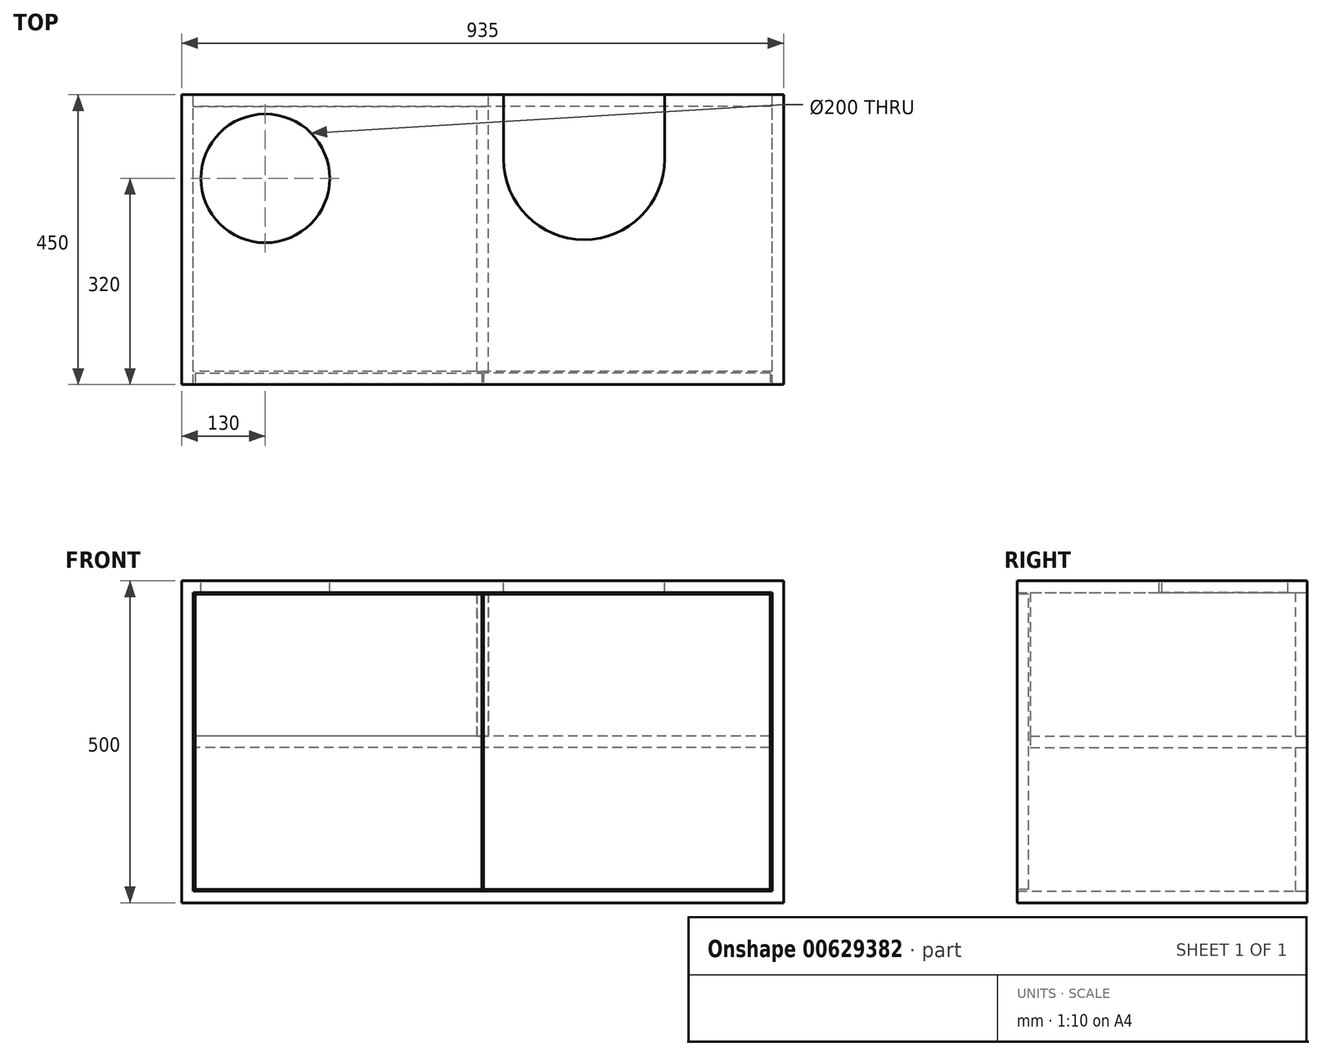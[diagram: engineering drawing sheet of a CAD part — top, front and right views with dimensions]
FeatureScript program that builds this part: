
annotation { "Feature Type Name" : "Feature", "Feature Type Description" : "" }
export const myFeature = defineFeature(function(context is Context, id is Id, definition is map)
    precondition{}
    {
        {
            var Q0;
            Q0=qCreatedBy(makeId("Front.planeOp"),FACE);
            var sketch = newSketch(context, id + "F0", { "sketchPlane" : qUnion([Q0])});
            skLineSegment(sketch, "E0.bottom", {"start": v(-467.5, 250) * mm, "end": v(467.5, 250) * mm});
            skLineSegment(sketch, "E0.top", {"start": v(-467.5, -250) * mm, "end": v(467.5, -250) * mm});
            skLineSegment(sketch, "E0.left", {"start": v(-467.5, 250) * mm, "end": v(-467.5, -250) * mm});
            skLineSegment(sketch, "E0.right", {"start": v(467.5, 250) * mm, "end": v(467.5, -250) * mm});
            skPoint(sketch, "E0.middle", {"position": v(0, 0) * mm});
            skLineSegment(sketch, "E1.0", {"start": v(449.5, 232) * mm, "end": v(449.5, -232) * mm});
            skLineSegment(sketch, "E1.1", {"start": v(-449.5, 232) * mm, "end": v(449.5, 232) * mm});
            skLineSegment(sketch, "E1.2", {"start": v(-449.5, 232) * mm, "end": v(-449.5, -232) * mm});
            skLineSegment(sketch, "E1.3", {"start": v(-449.5, -232) * mm, "end": v(449.5, -232) * mm});
            skSolve(sketch);
        }
        {
            var Q0;
            Q0 = qSketchRegion(id + "F0", true);
            extrude(context, id + "F1", {"entities" : qUnion([Q0]), "depth" : 450 * mm, "offsetDistance" : 25 * mm});
        }
        {
            var Q0;
            Q0=makeQuery(id+"F1.opExtrude","CAP_FACE",FACE,{"disambiguationData":[OSD([sQuery(id+"F0.wireOp",EDGE,"E0.bottom"),sQuery(id+"F0.wireOp",EDGE,"E0.top"),sQuery(id+"F0.wireOp",EDGE,"E0.left"),sQuery(id+"F0.wireOp",EDGE,"E0.right"),sQuery(id+"F0.wireOp",EDGE,"E1.0"),sQuery(id+"F0.wireOp",EDGE,"E1.1"),sQuery(id+"F0.wireOp",EDGE,"E1.2"),sQuery(id+"F0.wireOp",EDGE,"E1.3")])],"isStart":true});
            var sketch = newSketch(context, id + "F2", { "sketchPlane" : qUnion([Q0])});
            skLineSegment(sketch, "E2", {"start": v(-449.5, 0) * mm, "end": v(449.5, 0) * mm, "construction": true});
            skLineSegment(sketch, "E3.bottom", {"start": v(-449.5, 9) * mm, "end": v(449.5, 9) * mm});
            skLineSegment(sketch, "E3.top", {"start": v(-449.5, -9) * mm, "end": v(449.5, -9) * mm});
            skLineSegment(sketch, "E3.left", {"start": v(-449.5, 9) * mm, "end": v(-449.5, -9) * mm});
            skLineSegment(sketch, "E3.right", {"start": v(449.5, 9) * mm, "end": v(449.5, -9) * mm});
            skPoint(sketch, "E3.middle", {"position": v(0, 0) * mm});
            skSolve(sketch);
        }
        {
            var Q0;
            Q0 = qSketchRegion(id + "F2", true);
            extrude(context, id + "F3", {"entities" : qUnion([Q0]), "operationType" : NewBodyOperationType.ADD, "oppositeDirection" : true, "depth" : 430 * mm, "offsetDistance" : 25 * mm});
        }
        {
            var Q0;
            Q0=makeQuery(id+"F1.opExtrude","SWEPT_FACE",FACE,{"disambiguationData":[OSD([sQuery(id+"F0.wireOp",EDGE,"E0.bottom")])]});
            var sketch = newSketch(context, id + "F4", { "sketchPlane" : qUnion([Q0])});
            skCircle(sketch, "E4", {"center": v(-337.5, -130) * mm, "radius": 100 * mm});
            skSolve(sketch);
        }
        {
            var Q0;
            Q0 = qSketchRegion(id + "F4", true);
            var Q1;
            Q1=makeQuery(id+"F1.opExtrude","SWEPT_FACE",FACE,{"disambiguationData":[OSD([sQuery(id+"F0.wireOp",EDGE,"E1.1")])]});
            extrude(context, id + "F5", {"entities" : qUnion([Q0]), "operationType" : NewBodyOperationType.REMOVE, "endBound" : BoundingType.UP_TO_SURFACE, "oppositeDirection" : true, "depth" : 25 * mm, "endBoundEntityFace" : qUnion([Q1]), "offsetDistance" : 25 * mm});
        }
        {
            var Q0;
            Q0=makeQuery(id+"F1.opExtrude","SWEPT_FACE",FACE,{"disambiguationData":[OSD([sQuery(id+"F0.wireOp",EDGE,"E0.bottom")])]});
            var sketch = newSketch(context, id + "F6", { "sketchPlane" : qUnion([Q0])});
            skLineSegment(sketch, "E5", {"start": v(157.5, 0) * mm, "end": v(157.5, -200) * mm, "construction": true});
            skLineSegment(sketch, "E6", {"start": v(257.5, 0) * mm, "end": v(257.5, -60) * mm, "construction": true});
            skLineSegment(sketch, "E7", {"start": v(57.5, 0) * mm, "end": v(57.5, -60) * mm, "construction": true});
            skArc(sketch, "E8", {"start": v(132.5, -200) * mm, "mid": v(157.5, -225) * mm, "end": v(182.5, -200) * mm, "construction": true});
            skArc(sketch, "E9", {"start": v(232.5, -60) * mm, "mid": v(257.5, -85) * mm, "end": v(282.5, -60) * mm, "construction": true});
            skArc(sketch, "E10", {"start": v(32.5, -60) * mm, "mid": v(57.5, -85) * mm, "end": v(82.5, -60) * mm, "construction": true});
            skLineSegment(sketch, "E11", {"start": v(132.5, -200) * mm, "end": v(182.5, -200) * mm, "construction": true});
            skLineSegment(sketch, "E12", {"start": v(232.5, -60) * mm, "end": v(282.5, -60) * mm, "construction": true});
            skLineSegment(sketch, "E13", {"start": v(32.5, -60) * mm, "end": v(82.5, -60) * mm, "construction": true});
            skLineSegment(sketch, "E14", {"start": v(32.5, 0) * mm, "end": v(32.5, -60) * mm, "construction": true});
            skLineSegment(sketch, "E15", {"start": v(82.5, -60) * mm, "end": v(82.5, 0) * mm, "construction": true});
            skLineSegment(sketch, "E16", {"start": v(82.5, 0) * mm, "end": v(32.5, 0) * mm, "construction": true});
            skLineSegment(sketch, "E17", {"start": v(232.5, -60) * mm, "end": v(232.5, 0) * mm, "construction": true});
            skLineSegment(sketch, "E18", {"start": v(232.5, 0) * mm, "end": v(282.5, 0) * mm, "construction": true});
            skLineSegment(sketch, "E19", {"start": v(282.5, 0) * mm, "end": v(282.5, -60) * mm, "construction": true});
            skLineSegment(sketch, "E20", {"start": v(132.5, -200) * mm, "end": v(132.5, 0) * mm, "construction": true});
            skLineSegment(sketch, "E21", {"start": v(132.5, 0) * mm, "end": v(182.5, 0) * mm, "construction": true});
            skLineSegment(sketch, "E22", {"start": v(182.5, 0) * mm, "end": v(182.5, -200) * mm, "construction": true});
            skPoint(sketch, "E23.orphan", {"position": v(257.5, -85) * mm});
            skPoint(sketch, "E24.start.orphan", {"position": v(57.5, -85) * mm});
            skLineSegment(sketch, "E25", {"start": v(32.5, 0) * mm, "end": v(32.5, -60) * mm});
            skLineSegment(sketch, "E26", {"start": v(282.5, -60) * mm, "end": v(282.5, 0) * mm});
            skLineSegment(sketch, "E27", {"start": v(282.5, 0) * mm, "end": v(32.5, 0) * mm});
            skPoint(sketch, "E28.orphan", {"position": v(157.5, -225) * mm});
            skArc(sketch, "E29", {"start": v(32.5, -100) * mm, "mid": v(157.5, -225) * mm, "end": v(282.5, -100) * mm});
            skLineSegment(sketch, "E30", {"start": v(32.5, -60) * mm, "end": v(32.5, -100) * mm});
            skLineSegment(sketch, "E31", {"start": v(282.5, -60) * mm, "end": v(282.5, -100) * mm});
            skSolve(sketch);
        }
        {
            var Q0;
            Q0 = qSketchRegion(id + "F6", true);
            var Q1;
            Q1=makeQuery(id+"F1.opExtrude","SWEPT_FACE",FACE,{"disambiguationData":[OSD([sQuery(id+"F0.wireOp",EDGE,"E1.1")])]});
            extrude(context, id + "F7", {"entities" : qUnion([Q0]), "operationType" : NewBodyOperationType.REMOVE, "endBound" : BoundingType.UP_TO_SURFACE, "oppositeDirection" : true, "depth" : 25 * mm, "endBoundEntityFace" : qUnion([Q1]), "offsetDistance" : 25 * mm});
        }
        {
            var Q0;
            Q0=makeQuery(id+"F1.opExtrude","CAP_FACE",FACE,{"disambiguationData":[OSD([sQuery(id+"F0.wireOp",EDGE,"E0.bottom"),sQuery(id+"F0.wireOp",EDGE,"E0.top"),sQuery(id+"F0.wireOp",EDGE,"E0.left"),sQuery(id+"F0.wireOp",EDGE,"E0.right"),sQuery(id+"F0.wireOp",EDGE,"E1.0"),sQuery(id+"F0.wireOp",EDGE,"E1.1"),sQuery(id+"F0.wireOp",EDGE,"E1.2"),sQuery(id+"F0.wireOp",EDGE,"E1.3")])],"isStart":false});
            var sketch = newSketch(context, id + "F8", { "sketchPlane" : qUnion([Q0])});
            skLineSegment(sketch, "E32.0", {"start": v(-446.5, 229) * mm, "end": v(-446.5, -229) * mm, "construction": true});
            skLineSegment(sketch, "E32.1", {"start": v(-446.5, 229) * mm, "end": v(446.5, 229) * mm, "construction": true});
            skLineSegment(sketch, "E32.2", {"start": v(446.5, 229) * mm, "end": v(446.5, -229) * mm, "construction": true});
            skLineSegment(sketch, "E32.3", {"start": v(-446.5, -229) * mm, "end": v(446.5, -229) * mm, "construction": true});
            skLineSegment(sketch, "E33.bottom", {"start": v(446.5, -229) * mm, "end": v(1.5, -229) * mm});
            skLineSegment(sketch, "E33.top", {"start": v(446.5, 229) * mm, "end": v(1.5, 229) * mm});
            skLineSegment(sketch, "E33.left", {"start": v(446.5, -229) * mm, "end": v(446.5, 229) * mm});
            skLineSegment(sketch, "E33.right", {"start": v(1.5, -229) * mm, "end": v(1.5, 229) * mm});
            skLineSegment(sketch, "E34.bottom", {"start": v(-446.5, -229) * mm, "end": v(-1.5, -229) * mm});
            skLineSegment(sketch, "E34.top", {"start": v(-446.5, 229) * mm, "end": v(-1.5, 229) * mm});
            skLineSegment(sketch, "E34.left", {"start": v(-446.5, -229) * mm, "end": v(-446.5, 229) * mm});
            skLineSegment(sketch, "E34.right", {"start": v(-1.5, -229) * mm, "end": v(-1.5, 229) * mm});
            skLineSegment(sketch, "E35", {"start": v(0, 250) * mm, "end": v(0, -250) * mm, "construction": true});
            skSolve(sketch);
        }
        {
            var Q0;
            Q0 = qSketchRegion(id + "F8", true);
            extrude(context, id + "F9", {"entities" : qUnion([Q0]), "oppositeDirection" : true, "depth" : 18 * mm, "offsetDistance" : 25 * mm});
        }
        {
            var Q0;
            Q0=makeQuery(id+"F3.boolean.opBoolean","MERGE",FACE,{"derivedFrom":[makeQuery(id+"F1.opExtrude","CAP_FACE",FACE,{"disambiguationData":[OSD([sQuery(id+"F0.wireOp",EDGE,"E0.bottom"),sQuery(id+"F0.wireOp",EDGE,"E0.top"),sQuery(id+"F0.wireOp",EDGE,"E0.left"),sQuery(id+"F0.wireOp",EDGE,"E0.right"),sQuery(id+"F0.wireOp",EDGE,"E1.0"),sQuery(id+"F0.wireOp",EDGE,"E1.1"),sQuery(id+"F0.wireOp",EDGE,"E1.2"),sQuery(id+"F0.wireOp",EDGE,"E1.3")])],"isStart":true}),makeQuery(id+"F3.opExtrude","CAP_FACE",FACE,{"disambiguationData":[OSD([sQuery(id+"F2.wireOp",EDGE,"E3.bottom"),sQuery(id+"F2.wireOp",EDGE,"E3.top"),sQuery(id+"F2.wireOp",EDGE,"E3.left"),sQuery(id+"F2.wireOp",EDGE,"E3.right")])],"isStart":true})]});
            var sketch = newSketch(context, id + "F10", { "sketchPlane" : qUnion([Q0])});
            skLineSegment(sketch, "E36.bottom", {"start": v(449.5, -232) * mm, "end": v(-449.5, -232) * mm});
            skLineSegment(sketch, "E36.top", {"start": v(449.5, -9) * mm, "end": v(-449.5, -9) * mm});
            skLineSegment(sketch, "E36.left", {"start": v(449.5, -232) * mm, "end": v(449.5, -9) * mm});
            skLineSegment(sketch, "E36.right", {"start": v(-449.5, -232) * mm, "end": v(-449.5, -9) * mm});
            skPoint(sketch, "E37.startSnap0", {"position": v(0, 9) * mm});
            skPoint(sketch, "E38.orphan", {"position": v(9, 9) * mm});
            skPoint(sketch, "E39.top.start.orphan", {"position": v(-9, 9) * mm});
            skPoint(sketch, "E37.start.orphan", {"position": v(0, -250) * mm});
            skLineSegment(sketch, "E40", {"start": v(0, -250) * mm, "end": v(0, 232) * mm, "construction": true});
            skLineSegment(sketch, "E41", {"start": v(-9, 9) * mm, "end": v(-9, 232) * mm, "construction": true});
            skLineSegment(sketch, "E42.bottom", {"start": v(-9, 232) * mm, "end": v(449.5, 232) * mm});
            skLineSegment(sketch, "E42.top", {"start": v(-9, 9) * mm, "end": v(449.5, 9) * mm});
            skLineSegment(sketch, "E42.left", {"start": v(-9, 232) * mm, "end": v(-9, 9) * mm});
            skLineSegment(sketch, "E42.right", {"start": v(449.5, 232) * mm, "end": v(449.5, 9) * mm});
            skSolve(sketch);
        }
        {
            var Q0;
            Q0 = qSketchRegion(id + "F10", true);
            extrude(context, id + "F11", {"entities" : qUnion([Q0]), "oppositeDirection" : true, "depth" : 18 * mm, "offsetDistance" : 25 * mm});
        }
        {
            var Q0;
            Q0=makeQuery(id+"F11.opExtrude","CAP_FACE",FACE,{"disambiguationData":[OSD([sQuery(id+"F10.wireOp",EDGE,"E42.bottom"),sQuery(id+"F10.wireOp",EDGE,"E42.top"),sQuery(id+"F10.wireOp",EDGE,"E42.left"),sQuery(id+"F10.wireOp",EDGE,"E42.right")])],"isStart":false});
            var sketch = newSketch(context, id + "F12", { "sketchPlane" : qUnion([Q0])});
            skLineSegment(sketch, "E43.bottom", {"start": v(-9, 9) * mm, "end": v(9, 9) * mm});
            skLineSegment(sketch, "E43.top", {"start": v(-9, 232) * mm, "end": v(9, 232) * mm});
            skLineSegment(sketch, "E43.left", {"start": v(-9, 9) * mm, "end": v(-9, 232) * mm});
            skLineSegment(sketch, "E43.right", {"start": v(9, 9) * mm, "end": v(9, 232) * mm});
            skSolve(sketch);
        }
        {
            var Q0;
            Q0 = qSketchRegion(id + "F12", true);
            var Q1;
            Q1=makeQuery(id+"F3.opExtrude","CAP_FACE",FACE,{"disambiguationData":[OSD([sQuery(id+"F2.wireOp",EDGE,"E3.bottom"),sQuery(id+"F2.wireOp",EDGE,"E3.top"),sQuery(id+"F2.wireOp",EDGE,"E3.left"),sQuery(id+"F2.wireOp",EDGE,"E3.right")])],"isStart":false});
            extrude(context, id + "F13", {"entities" : qUnion([Q0]), "endBound" : BoundingType.UP_TO_SURFACE, "depth" : 25 * mm, "endBoundEntityFace" : qUnion([Q1]), "offsetDistance" : 25 * mm});
        }
    });
